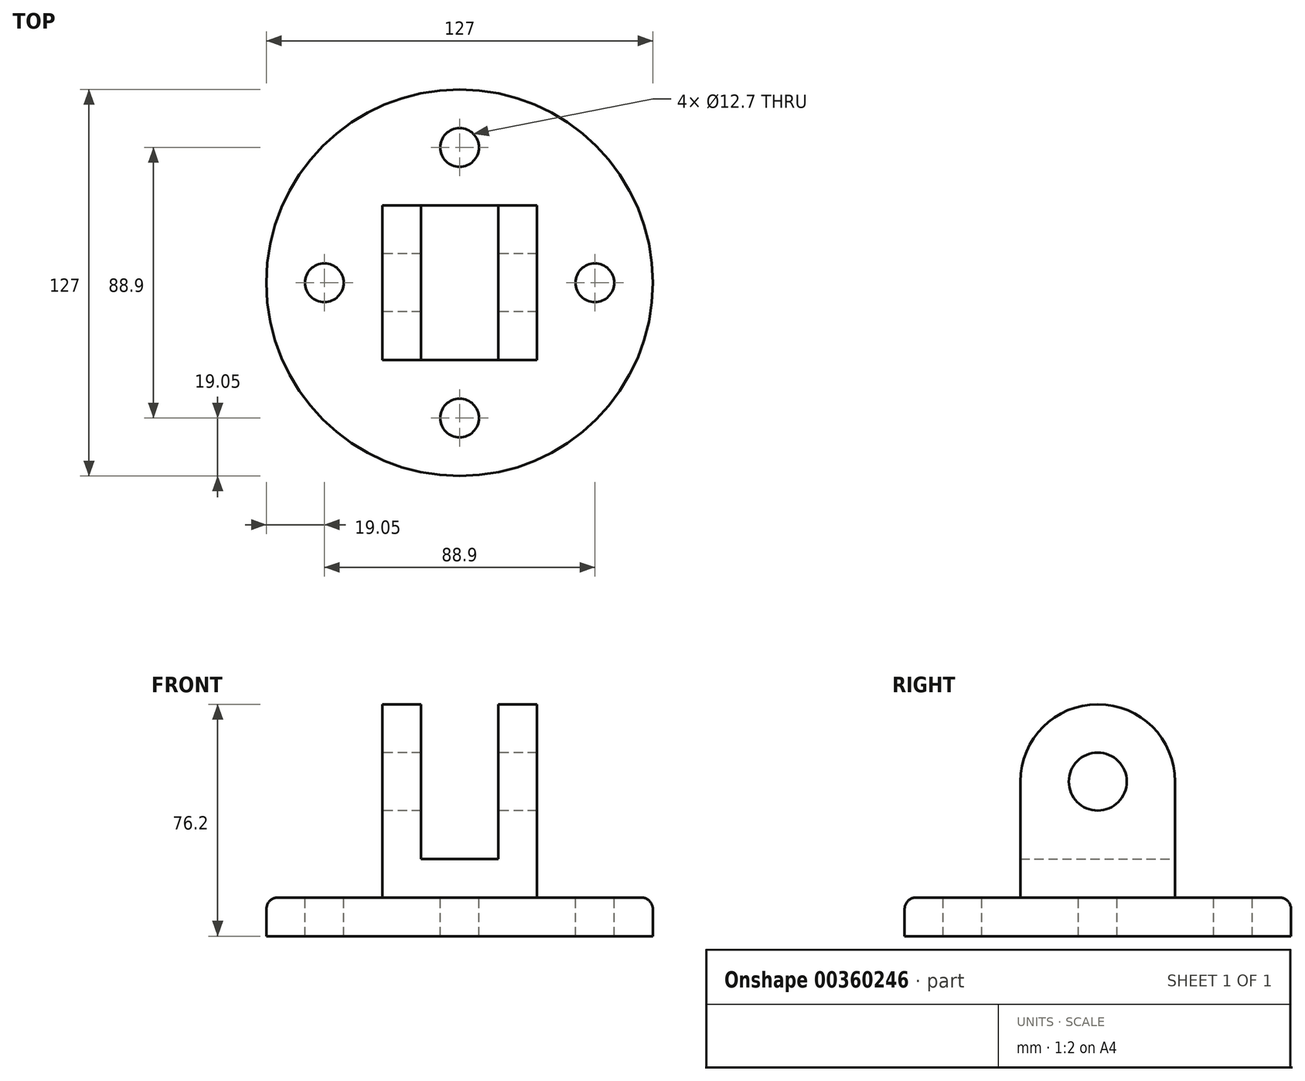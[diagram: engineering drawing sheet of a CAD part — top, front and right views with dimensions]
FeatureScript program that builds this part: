
annotation { "Feature Type Name" : "Feature", "Feature Type Description" : "" }
export const myFeature = defineFeature(function(context is Context, id is Id, definition is map)
    precondition{}
    {
        {
            var Q0;
            Q0=qCreatedBy(makeId("Top.planeOp"),FACE);
            var sketch = newSketch(context, id + "F0", { "sketchPlane" : qUnion([Q0])});
            skCircle(sketch, "E0", {"center": v(0, 0) * mm, "radius": 63.5 * mm});
            skSolve(sketch);
        }
        {
            var Q0;
            Q0=makeQuery(id+"F0.imprint","IMPRINT",FACE,{"disambiguationData":[TD([[makeQuery(id+"F0.imprint","IMPRINT",EDGE,{"derivedFrom":sQuery(id+"F0.wireOp",EDGE,"E0")}),1.0]])]});
            extrude(context, id + "F1", {"entities" : qUnion([Q0]), "depth" : 12.7 * mm, "symmetric" : true});
        }
        {
            var Q0;
            Q0=makeQuery(id+"F1.opExtrude","CAP_FACE",FACE,{"disambiguationData":[OSD([sQuery(id+"F0.wireOp",EDGE,"E0")])],"isStart":false});
            var sketch = newSketch(context, id + "F2", { "sketchPlane" : qUnion([Q0])});
            skCircle(sketch, "E1", {"center": v(0, 0) * mm, "radius": 44.45 * mm, "construction": true});
            skCircle(sketch, "E2", {"center": v(0, 44.45) * mm, "radius": 6.35 * mm});
            skCircle(sketch, "E3.1.0", {"center": v(44.45, 0) * mm, "radius": 6.35 * mm});
            skCircle(sketch, "E3.2.0", {"center": v(0, -44.45) * mm, "radius": 6.35 * mm});
            skCircle(sketch, "E3.3.0", {"center": v(-44.45, 0) * mm, "radius": 6.35 * mm});
            skLineSegment(sketch, "E3.anchor1", {"start": v(0, 0) * mm, "end": v(0, 44.45) * mm, "construction": true});
            skLineSegment(sketch, "E3.anchor2", {"start": v(0, 0) * mm, "end": v(-44.45, 0) * mm, "construction": true});
            skSolve(sketch);
        }
        {
            var Q0;
            Q0=makeQuery(id+"F2.imprint","IMPRINT",FACE,{"disambiguationData":[TD([[makeQuery(id+"F2.imprint","IMPRINT",EDGE,{"derivedFrom":sQuery(id+"F2.wireOp",EDGE,"E2")}),1.0]])]});
            var Q1;
            Q1=makeQuery(id+"F2.imprint","IMPRINT",FACE,{"disambiguationData":[TD([[makeQuery(id+"F2.imprint","IMPRINT",EDGE,{"derivedFrom":sQuery(id+"F2.wireOp",EDGE,"E3.1.0")}),1.0]])]});
            var Q2;
            Q2=makeQuery(id+"F2.imprint","IMPRINT",FACE,{"disambiguationData":[TD([[makeQuery(id+"F2.imprint","IMPRINT",EDGE,{"derivedFrom":sQuery(id+"F2.wireOp",EDGE,"E3.2.0")}),1.0]])]});
            var Q3;
            Q3=makeQuery(id+"F2.imprint","IMPRINT",FACE,{"disambiguationData":[TD([[makeQuery(id+"F2.imprint","IMPRINT",EDGE,{"derivedFrom":sQuery(id+"F2.wireOp",EDGE,"E3.3.0")}),1.0]])]});
            extrude(context, id + "F3", {"entities" : qUnion([Q0, Q1, Q2, Q3]), "operationType" : NewBodyOperationType.REMOVE, "endBound" : BoundingType.THROUGH_ALL, "oppositeDirection" : true, "depth" : 25.4 * mm});
        }
        {
            var Q0;
            Q0=qCreatedBy(makeId("Front.planeOp"),FACE);
            var sketch = newSketch(context, id + "F4", { "sketchPlane" : qUnion([Q0])});
            skLineSegment(sketch, "E4", {"start": v(26.51, 0) * mm, "end": v(-27.7, 0) * mm, "construction": true});
            skLineSegment(sketch, "E5.0", {"start": v(-63.5, -6.35) * mm, "end": v(63.5, -6.35) * mm});
            skLineSegment(sketch, "E6", {"start": v(0, -6.35) * mm, "end": v(0, 19.05) * mm, "construction": true});
            skPoint(sketch, "E6.endSnap0", {"position": v(0, -6.35) * mm});
            skLineSegment(sketch, "E7", {"start": v(-12.7, 19.05) * mm, "end": v(12.7, 19.05) * mm});
            skLineSegment(sketch, "E8.0", {"start": v(-63.5, 6.35) * mm, "end": v(63.5, 6.35) * mm});
            skLineSegment(sketch, "E9", {"start": v(-12.7, 19.05) * mm, "end": v(-12.7, 44.45) * mm});
            skLineSegment(sketch, "E10", {"start": v(-12.7, 44.45) * mm, "end": v(-25.4, 44.45) * mm});
            skLineSegment(sketch, "E11", {"start": v(-25.4, 44.45) * mm, "end": v(-25.4, 6.35) * mm});
            skLineSegment(sketch, "E12", {"start": v(12.7, 19.05) * mm, "end": v(12.7, 44.45) * mm});
            skLineSegment(sketch, "E13", {"start": v(12.7, 44.45) * mm, "end": v(25.4, 44.45) * mm});
            skLineSegment(sketch, "E14", {"start": v(25.4, 44.45) * mm, "end": v(25.4, 6.35) * mm});
            skSolve(sketch);
        }
        {
            var Q0;
            Q0=makeQuery(id+"F4.imprint","IMPRINT",FACE,{"disambiguationData":[TD([[makeQuery(id+"F4.imprint","IMPRINT",EDGE,{"derivedFrom":sQuery(id+"F4.wireOp",EDGE,"E7")}),-1.0]])]});
            extrude(context, id + "F5", {"entities" : qUnion([Q0]), "operationType" : NewBodyOperationType.ADD, "depth" : 50.8 * mm, "symmetric" : true});
        }
        {
            var Q0;
            Q0=makeQuery(id+"F5.opExtrude","SWEPT_FACE",FACE,{"disambiguationData":[OSD([sQuery(id+"F4.wireOp",EDGE,"E14")])]});
            var sketch = newSketch(context, id + "F6", { "sketchPlane" : qUnion([Q0])});
            skArc(sketch, "E15", {"start": v(25.4, 44.45) * mm, "mid": v(0, 69.85) * mm, "end": v(-25.4, 44.45) * mm});
            skSolve(sketch);
        }
        {
            var Q0;
            Q0 = qSketchRegion(id + "F6", true);
            var Q1;
            Q1=makeQuery(id+"F6.imprint","IMPRINT",FACE,{"disambiguationData":[TD([[makeQuery(id+"F6.imprint","IMPRINT",EDGE,{"derivedFrom":sQuery(id+"F6.wireOp",EDGE,"E15")}),1.0]])]});
            extrude(context, id + "F7", {"entities" : qUnion([Q0, Q1]), "operationType" : NewBodyOperationType.ADD, "oppositeDirection" : true, "depth" : 12.7 * mm});
        }
        {
            var Q0;
            Q0=makeQuery(id+"F5.opExtrude","SWEPT_FACE",FACE,{"disambiguationData":[OSD([sQuery(id+"F4.wireOp",EDGE,"E11")])]});
            var sketch = newSketch(context, id + "F8", { "sketchPlane" : qUnion([Q0])});
            skArc(sketch, "E16", {"start": v(25.4, 44.45) * mm, "mid": v(0, 69.85) * mm, "end": v(-25.4, 44.45) * mm});
            skCircle(sketch, "E17", {"center": v(0, 44.45) * mm, "radius": 9.53 * mm});
            skSolve(sketch);
        }
        {
            var Q0;
            Q0 = qSketchRegion(id + "F8", true);
            var Q1;
            Q1=makeQuery(id+"F8.imprint","IMPRINT",FACE,{"disambiguationData":[TD([[makeQuery(id+"F8.imprint","IMPRINT",EDGE,{"derivedFrom":sQuery(id+"F8.wireOp",EDGE,"E16")}),1.0]])]});
            extrude(context, id + "F9", {"entities" : qUnion([Q0, Q1]), "operationType" : NewBodyOperationType.ADD, "oppositeDirection" : true, "depth" : 12.7 * mm});
        }
        {
            var Q0;
            {var subQ0=sQuery(id+"F8.wireOp",EDGE,"E17");var subQ1=makeQuery(id+"F5.opExtrude","SWEPT_EDGE",EDGE,{"disambiguationData":[OSD([sQuery(id+"F4.wireOp",EDGE,"E10"),sQuery(id+"F4.wireOp",EDGE,"E11")])]});var subQ2=makeQuery(id+"F8.imprint","INTERSECT",VERTEX,{"disambiguationData":[OD(0.0)],"derivedFrom":[subQ1,subQ0]});Q0=makeQuery(id+"F8.imprint","IMPRINT",FACE,{"disambiguationData":[TD([[makeQuery(id+"F8.imprint","IMPRINT",EDGE,{"disambiguationData":[TD([[subQ2,-1.0]])],"derivedFrom":subQ0}),1.0]])]});}
            var Q1;
            {var subQ0=sQuery(id+"F8.wireOp",EDGE,"E17");var subQ1=makeQuery(id+"F5.opExtrude","SWEPT_EDGE",EDGE,{"disambiguationData":[OSD([sQuery(id+"F4.wireOp",EDGE,"E10"),sQuery(id+"F4.wireOp",EDGE,"E11")])]});var subQ2=makeQuery(id+"F8.imprint","INTERSECT",VERTEX,{"disambiguationData":[OD(0.0)],"derivedFrom":[subQ1,subQ0]});Q1=makeQuery(id+"F8.imprint","IMPRINT",FACE,{"disambiguationData":[TD([[makeQuery(id+"F8.imprint","IMPRINT",EDGE,{"disambiguationData":[TD([[subQ2,1.0]])],"derivedFrom":subQ0}),1.0]])]});}
            extrude(context, id + "F10", {"entities" : qUnion([Q0, Q1]), "operationType" : NewBodyOperationType.REMOVE, "endBound" : BoundingType.THROUGH_ALL, "oppositeDirection" : true, "depth" : 25.4 * mm});
        }
        {
            var Q0;
            Q0=makeQuery(id+"F5.opExtrude","CAP_EDGE",EDGE,{"disambiguationData":[OSD([sQuery(id+"F4.wireOp",EDGE,"E8.0")])],"isStart":false});
            var Q1;
            Q1=makeQuery(id+"F5.opExtrude","SWEPT_EDGE",EDGE,{"disambiguationData":[OSD([sQuery(id+"F4.wireOp",EDGE,"E8.0"),sQuery(id+"F4.wireOp",EDGE,"E11")])]});
            var Q2;
            Q2=makeQuery(id+"F5.opExtrude","CAP_EDGE",EDGE,{"disambiguationData":[OSD([sQuery(id+"F4.wireOp",EDGE,"E8.0")])],"isStart":true});
            var Q3;
            Q3=makeQuery(id+"F5.opExtrude","SWEPT_EDGE",EDGE,{"disambiguationData":[OSD([sQuery(id+"F4.wireOp",EDGE,"E8.0"),sQuery(id+"F4.wireOp",EDGE,"E14")])]});
            var Q4;
            Q4=makeQuery(id+"F1.opExtrude","CAP_EDGE",EDGE,{"disambiguationData":[OSD([sQuery(id+"F0.wireOp",EDGE,"E0")])],"isStart":false});
            fillet(context, id + "F11", {"entities" : qUnion([Q0, Q1, Q2, Q3, Q4]), "radius" : 3.8 * mm, "tangentPropagation" : true, "allowEdgeOverflow" : false});
        }
    });
